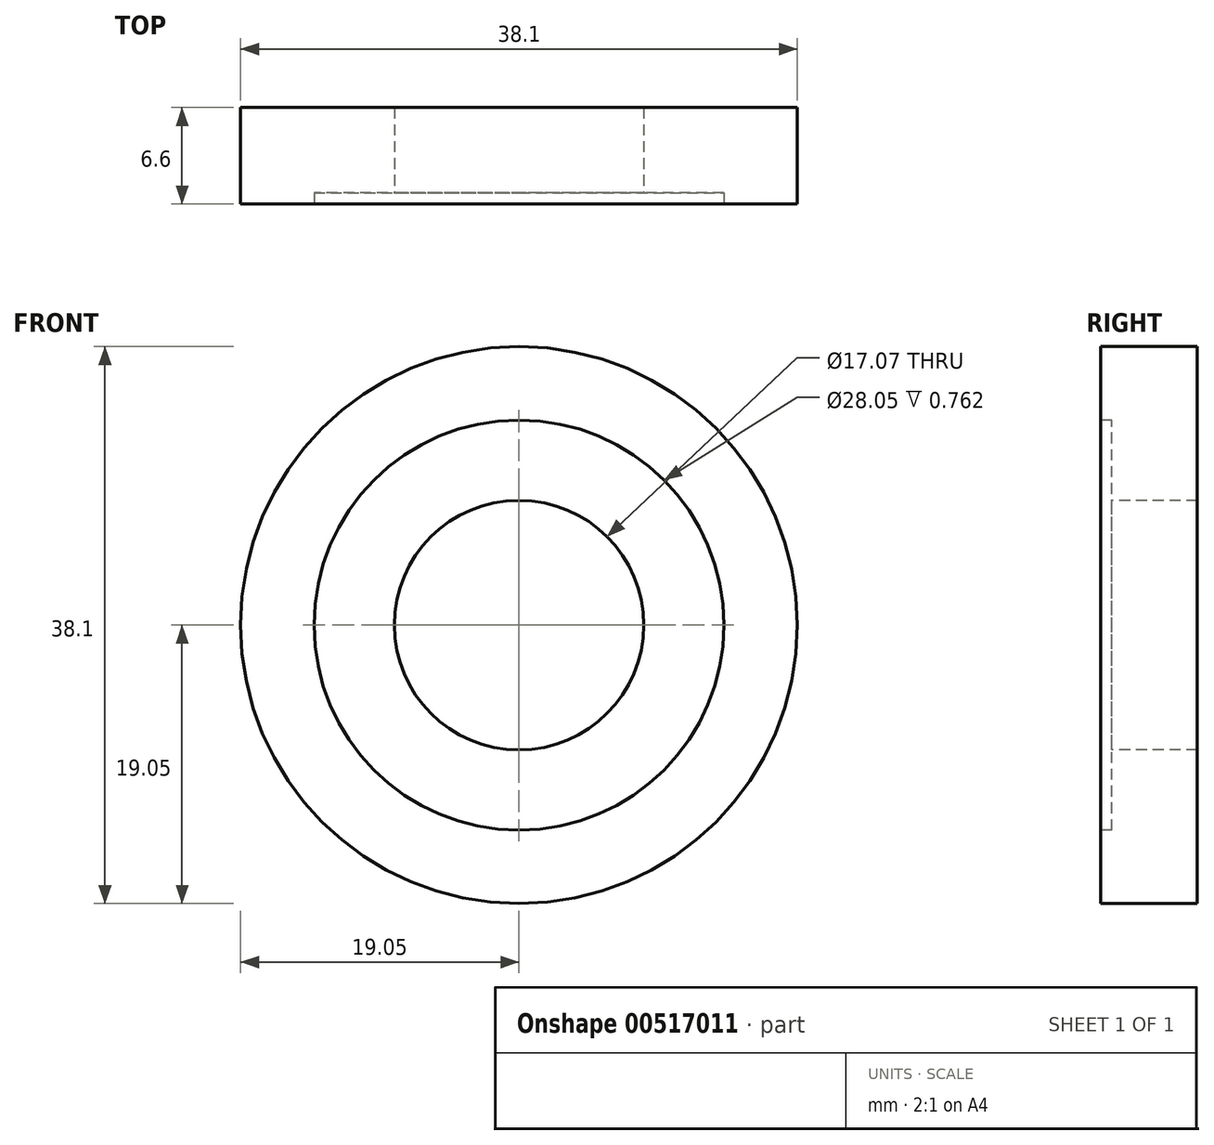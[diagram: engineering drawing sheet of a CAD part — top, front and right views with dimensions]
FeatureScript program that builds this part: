
annotation { "Feature Type Name" : "Feature", "Feature Type Description" : "" }
export const myFeature = defineFeature(function(context is Context, id is Id, definition is map)
    precondition{}
    {
        {
            var Q0;
            Q0=qCreatedBy(makeId("Front.planeOp"),FACE);
            var sketch = newSketch(context, id + "F0", { "sketchPlane" : qUnion([Q0])});
            skCircle(sketch, "E0", {"center": v(0, 0) * mm, "radius": 19.05 * mm});
            skSolve(sketch);
        }
        {
            var Q0;
            Q0 = qSketchRegion(id + "F0", true);
            extrude(context, id + "F1", {"entities" : qUnion([Q0]), "endBound" : BoundingType.SYMMETRIC, "depth" : 6.6 * mm, "offsetDistance" : 25.4 * mm});
        }
        {
            var Q0;
            Q0=makeQuery(id+"F1.opExtrude","CAP_FACE",FACE,{"disambiguationData":[OSD([sQuery(id+"F0.wireOp",EDGE,"E0")])],"isStart":false});
            var sketch = newSketch(context, id + "F2", { "sketchPlane" : qUnion([Q0])});
            skCircle(sketch, "E1", {"center": v(0, 0) * mm, "radius": 8.53 * mm});
            skSolve(sketch);
        }
        {
            var Q0;
            Q0=makeQuery(id+"F2.imprint","IMPRINT",FACE,{"disambiguationData":[TD([[makeQuery(id+"F2.imprint","IMPRINT",EDGE,{"derivedFrom":sQuery(id+"F2.wireOp",EDGE,"E1")}),1.0]])]});
            var Q1;
            Q1 = qSketchRegion(id + "F4", true);
            extrude(context, id + "F3", {"entities" : qUnion([Q0, Q1]), "operationType" : NewBodyOperationType.REMOVE, "endBound" : BoundingType.THROUGH_ALL, "oppositeDirection" : true, "depth" : 10.16 * mm, "offsetDistance" : 25.4 * mm});
        }
        {
            var Q0;
            Q0=makeQuery(id+"F1.opExtrude","CAP_FACE",FACE,{"disambiguationData":[OSD([sQuery(id+"F0.wireOp",EDGE,"E0")])],"isStart":false});
            var sketch = newSketch(context, id + "F4", { "sketchPlane" : qUnion([Q0])});
            skCircle(sketch, "E2", {"center": v(0, 0) * mm, "radius": 14.03 * mm});
            skSolve(sketch);
        }
        {
            var Q0;
            Q0=makeQuery(id+"F4.imprint","IMPRINT",FACE,{"disambiguationData":[TD([[makeQuery(id+"F4.imprint","IMPRINT",EDGE,{"derivedFrom":sQuery(id+"F4.wireOp",EDGE,"E2")}),1.0]])]});
            extrude(context, id + "F5", {"entities" : qUnion([Q0]), "operationType" : NewBodyOperationType.REMOVE, "oppositeDirection" : true, "depth" : 0.76 * mm, "offsetDistance" : 25.4 * mm});
        }
    });
